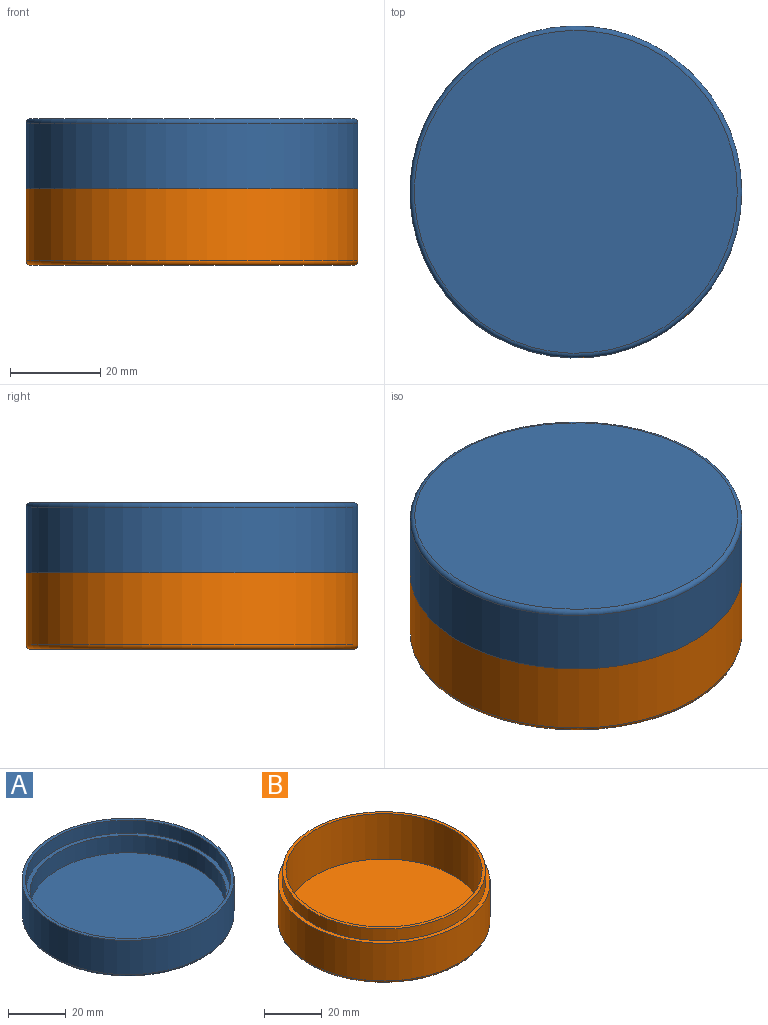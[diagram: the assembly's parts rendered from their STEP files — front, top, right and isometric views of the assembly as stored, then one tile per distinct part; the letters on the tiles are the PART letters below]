
ASSEMBLY  parts=2 mates=1
PART A: 8 faces, bbox 79.6x79.6x15.5 mm
  f0: cylinder r=36.75mm len=73.5mm, axis (0,0,-1), area 3348.2mm2, adj f1,f7
  f1: plane 73.5x73.5mm, normal (0,0,1), area 272.6mm2, adj f0,f3
  f2: plane 71.5x71.5mm, normal (0,0,-1), area 4015.2mm2, adj f7
  f3: cylinder r=35.55mm len=71.1mm, axis (0,0,1), area 1228.5mm2, adj f1,f4
  f4: plane 71.1x71.1mm, normal (0,0,1), area 338.7mm2, adj f3,f6
  f5: plane 68x68mm, normal (0,0,1), area 3631.7mm2, adj f6
  f6: cylinder r=34mm len=68mm, axis (0,0,-1), area 1548.8mm2, adj f4,f5
  f7: torus R=35.75mm, axis (0,0,1), area 359.1mm2, adj f0,f2
PART B: 8 faces, bbox 79.6x79.6x22 mm
  f0: cylinder r=36.75mm len=73.5mm, axis (0,0,-1), area 3694.5mm2, adj f1,f7
  f1: plane 73.5x73.5mm, normal (0,0,1), area 350.4mm2, adj f0,f3
  f2: plane 71.5x71.5mm, normal (0,0,-1), area 4015.2mm2, adj f7
  f3: cylinder r=35.2mm len=70.4mm, axis (0,0,-1), area 1105.8mm2, adj f1,f4
  f4: plane 70.4x70.4mm, normal (0,0,1), area 260.9mm2, adj f3,f6
  f5: plane 68x68mm, normal (0,0,1), area 3631.7mm2, adj f6
  f6: cylinder r=34mm len=68mm, axis (0,0,-1), area 4112.3mm2, adj f4,f5
  f7: torus R=35.75mm, axis (0,0,1), area 359.1mm2, adj f0,f2
PLACE A rot(axis=(1,0,0),180deg) t=(0.28,-0.83,14.51)mm
PLACE B t=(0.28,-0.83,-17.99)mm
MATE fastened A.f0 <-> B.f0  axis (0,0,-1) through (0.28,-0.83,-0.99)mm
